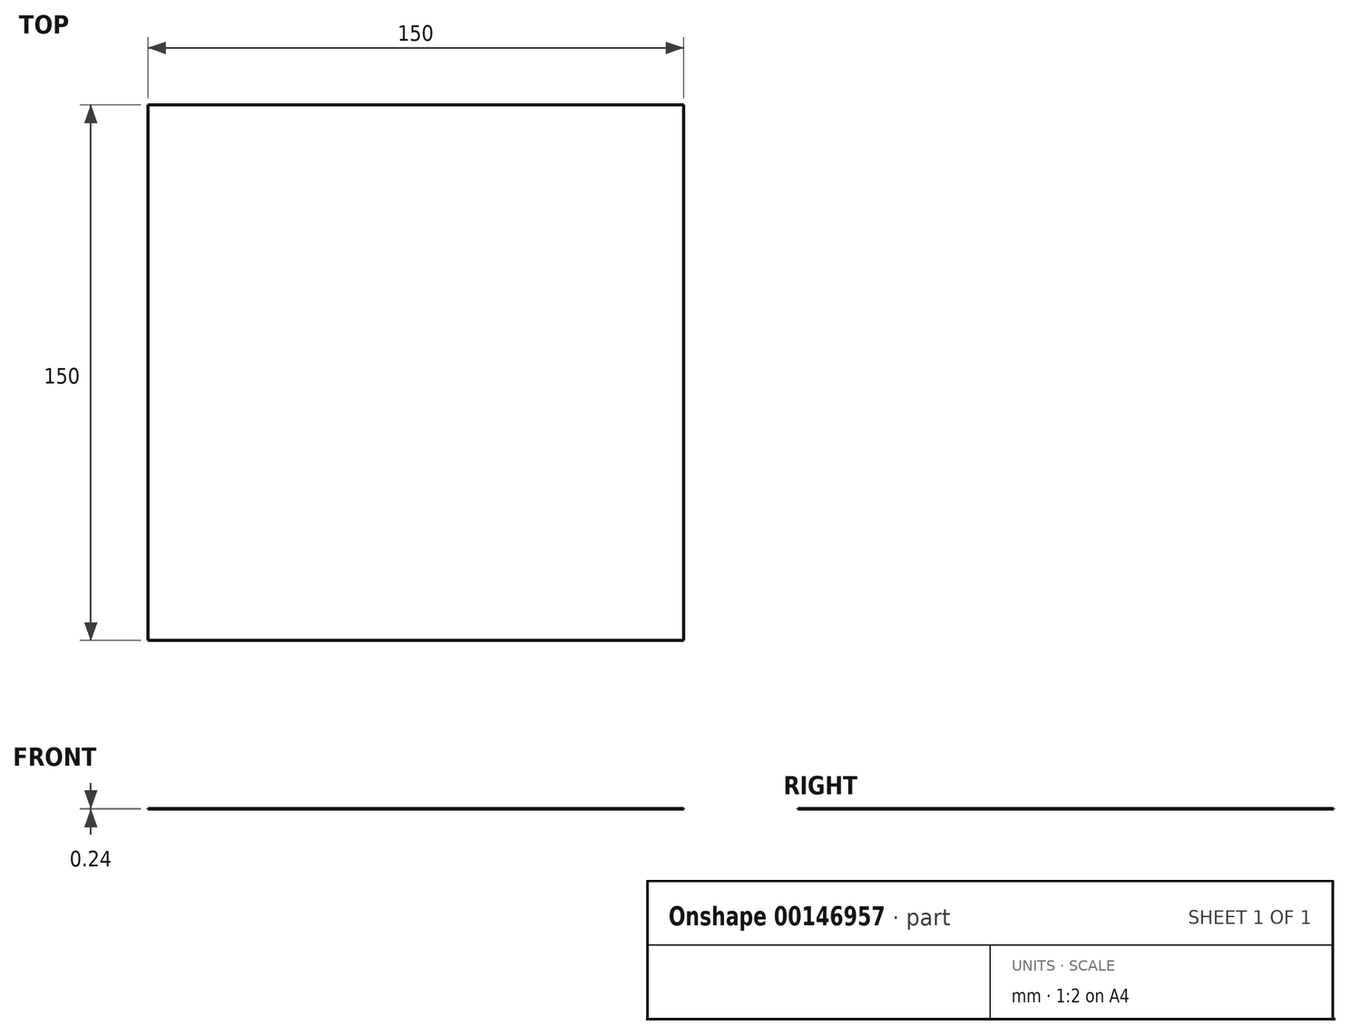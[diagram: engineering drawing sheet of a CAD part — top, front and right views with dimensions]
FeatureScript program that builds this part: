
annotation { "Feature Type Name" : "Feature", "Feature Type Description" : "" }
export const myFeature = defineFeature(function(context is Context, id is Id, definition is map)
    precondition{}
    {
        {
            var Q0;
            Q0=qCreatedBy(makeId("Top.planeOp"),FACE);
            var sketch = newSketch(context, id + "F0", { "sketchPlane" : qUnion([Q0])});
            skLineSegment(sketch, "E0.bottom", {"start": v(0, 0) * mm, "end": v(150, 0) * mm});
            skLineSegment(sketch, "E0.top", {"start": v(0, 150) * mm, "end": v(150, 150) * mm});
            skLineSegment(sketch, "E0.left", {"start": v(0, 0) * mm, "end": v(0, 150) * mm});
            skLineSegment(sketch, "E0.right", {"start": v(150, 0) * mm, "end": v(150, 150) * mm});
            skSolve(sketch);
        }
        {
            var Q0;
            Q0 = qSketchRegion(id + "F0", true);
            extrude(context, id + "F1", {"entities" : qUnion([Q0]), "depth" : 0.24 * mm});
        }
    });
